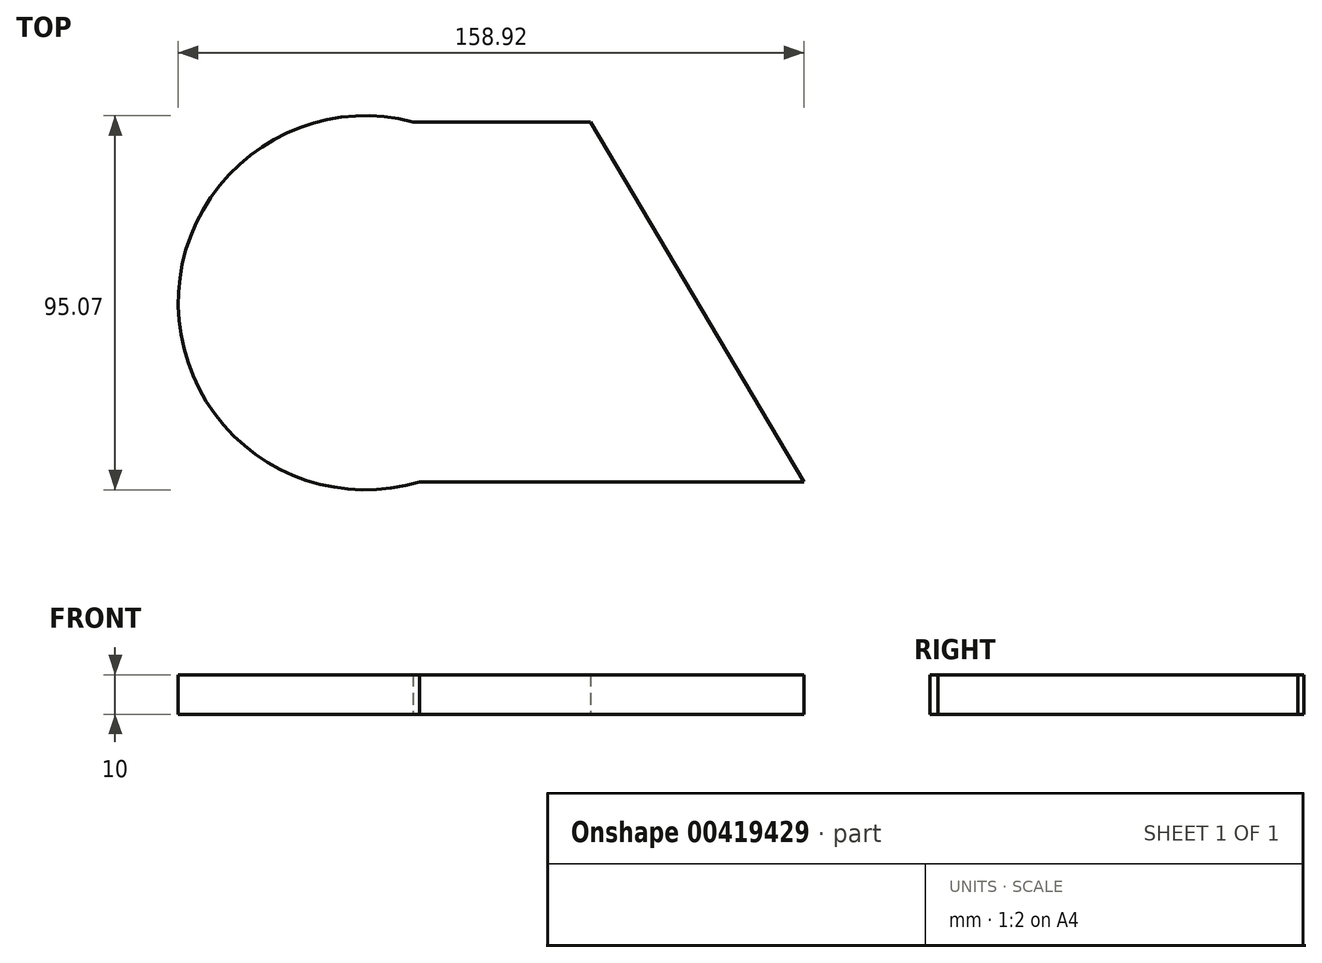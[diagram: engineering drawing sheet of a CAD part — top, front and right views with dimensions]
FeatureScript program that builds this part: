
annotation { "Feature Type Name" : "Feature", "Feature Type Description" : "" }
export const myFeature = defineFeature(function(context is Context, id is Id, definition is map)
    precondition{}
    {
        {
            var Q0;
            Q0=qCreatedBy(makeId("Top.planeOp"),FACE);
            var sketch = newSketch(context, id + "F0", { "sketchPlane" : qUnion([Q0])});
            skArc(sketch, "E0", {"start": v(-27.43, 47.7) * mm, "mid": v(-87.1, 0.88) * mm, "end": v(-25.76, -43.74) * mm});
            skLineSegment(sketch, "E1.bottom", {"start": v(-27.43, 47.7) * mm, "end": v(17.68, 47.7) * mm});
            skLineSegment(sketch, "E1.top", {"start": v(-27.43, -43.74) * mm, "end": v(17.68, -43.74) * mm});
            skPoint(sketch, "E2", {"position": v(76.2, 0) * mm});
            skPoint(sketch, "E3", {"position": v(75.9, 0.46) * mm});
            skLineSegment(sketch, "E4", {"start": v(17.68, 47.7) * mm, "end": v(71.81, -43.76) * mm});
            skLineSegment(sketch, "E5", {"start": v(71.81, -43.76) * mm, "end": v(17.68, -43.74) * mm});
            skSolve(sketch);
        }
        {
            var Q0;
            {var subQ1=sQuery(id+"F0.wireOp",EDGE,"E0");Q0=makeQuery(id+"F0.imprint","IMPRINT",FACE,{"disambiguationData":[TD([[makeQuery(id+"F0.imprint","IMPRINT",EDGE,{"derivedFrom":subQ1}),1.0]])]});}
            extrude(context, id + "F1", {"entities" : qUnion([Q0]), "depth" : 10 * mm});
        }
    });
